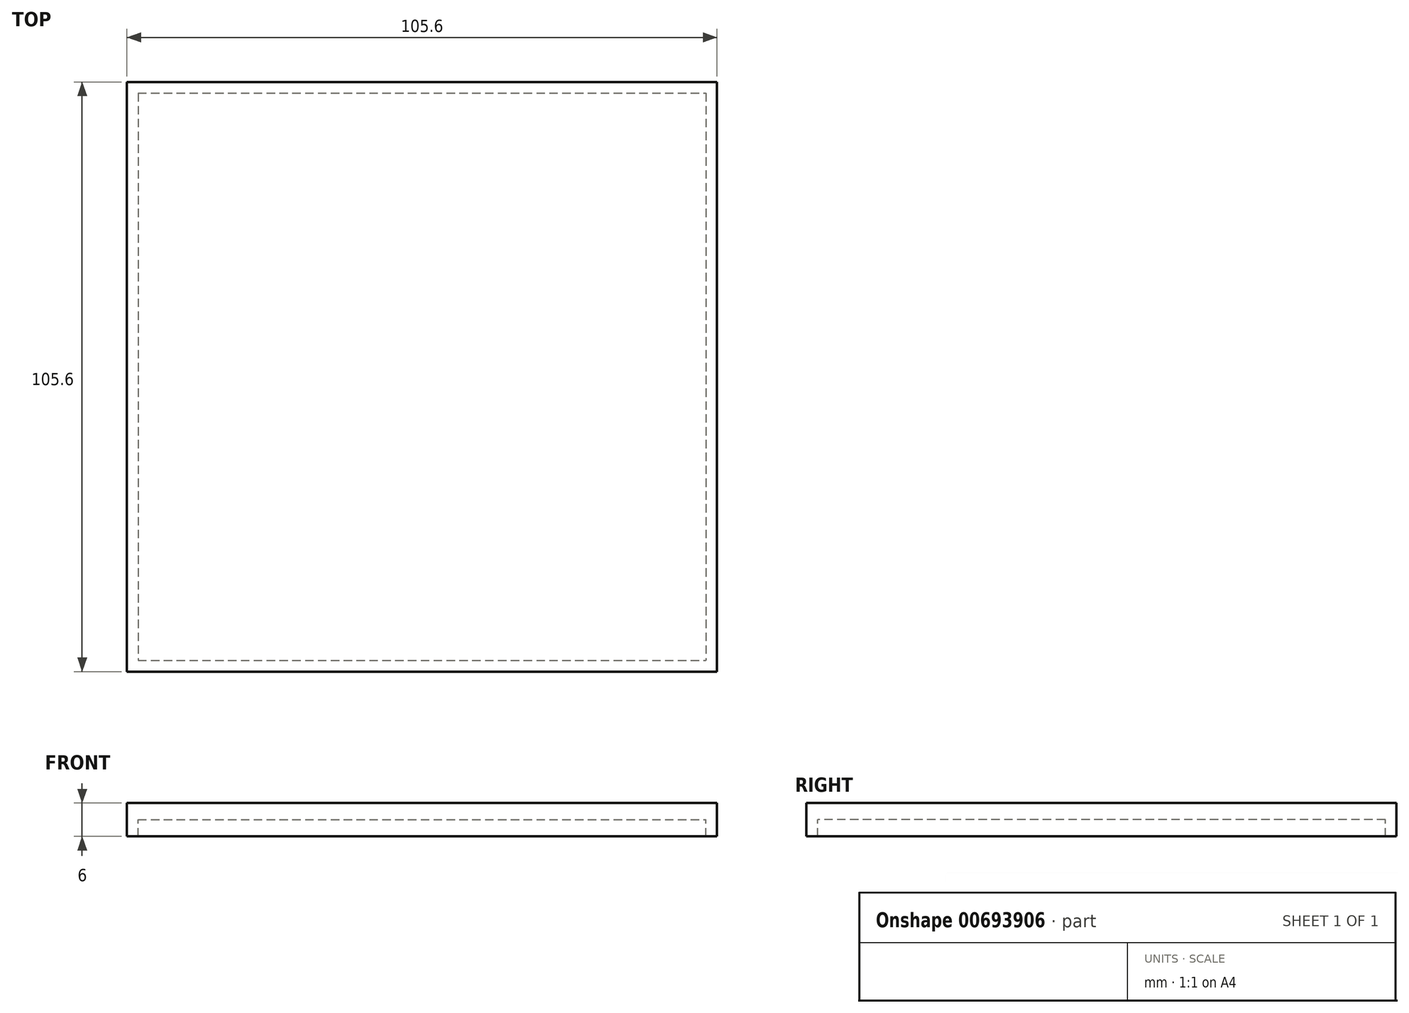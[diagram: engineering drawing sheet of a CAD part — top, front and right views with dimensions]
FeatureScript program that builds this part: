
annotation { "Feature Type Name" : "Feature", "Feature Type Description" : "" }
export const myFeature = defineFeature(function(context is Context, id is Id, definition is map)
    precondition{}
    {
        {
            var Q0;
            Q0=qCreatedBy(makeId("Top.planeOp"),FACE);
            var sketch = newSketch(context, id + "F0", { "sketchPlane" : qUnion([Q0])});
            skLineSegment(sketch, "E0.bottom", {"start": v(-50.8, 50.8) * mm, "end": v(50.8, 50.8) * mm});
            skLineSegment(sketch, "E0.top", {"start": v(-50.8, -50.8) * mm, "end": v(50.8, -50.8) * mm});
            skLineSegment(sketch, "E0.left", {"start": v(-50.8, 50.8) * mm, "end": v(-50.8, -50.8) * mm});
            skLineSegment(sketch, "E0.right", {"start": v(50.8, 50.8) * mm, "end": v(50.8, -50.8) * mm});
            skPoint(sketch, "E0.middle", {"position": v(0, 0) * mm});
            skLineSegment(sketch, "E1.0", {"start": v(-52.8, 52.8) * mm, "end": v(-52.8, -52.8) * mm});
            skLineSegment(sketch, "E1.1", {"start": v(-52.8, 52.8) * mm, "end": v(52.8, 52.8) * mm});
            skLineSegment(sketch, "E1.2", {"start": v(52.8, 52.8) * mm, "end": v(52.8, -52.8) * mm});
            skLineSegment(sketch, "E1.3", {"start": v(-52.8, -52.8) * mm, "end": v(52.8, -52.8) * mm});
            skSolve(sketch);
        }
        {
            var Q0;
            Q0=makeQuery(id+"F0.imprint","IMPRINT",FACE,{"disambiguationData":[TD([[makeQuery(id+"F0.imprint","IMPRINT",EDGE,{"derivedFrom":sQuery(id+"F0.wireOp",EDGE,"E0.bottom")}),1.0]])]});
            extrude(context, id + "F1", {"entities" : qUnion([Q0]), "oppositeDirection" : true, "depth" : 3 * mm, "offsetDistance" : 25.4 * mm});
        }
        {
            var Q0;
            Q0=qCreatedBy(makeId("Top.planeOp"),FACE);
            var sketch = newSketch(context, id + "F2", { "sketchPlane" : qUnion([Q0])});
            skLineSegment(sketch, "E2.bottom", {"start": v(-52.8, -52.8) * mm, "end": v(52.8, -52.8) * mm});
            skLineSegment(sketch, "E2.top", {"start": v(-52.8, 52.8) * mm, "end": v(52.8, 52.8) * mm});
            skLineSegment(sketch, "E2.left", {"start": v(-52.8, -52.8) * mm, "end": v(-52.8, 52.8) * mm});
            skLineSegment(sketch, "E2.right", {"start": v(52.8, -52.8) * mm, "end": v(52.8, 52.8) * mm});
            skSolve(sketch);
        }
        {
            var Q0;
            Q0 = qSketchRegion(id + "F2", true);
            extrude(context, id + "F3", {"entities" : qUnion([Q0]), "operationType" : NewBodyOperationType.ADD, "depth" : 3 * mm, "offsetDistance" : 25.4 * mm});
        }
    });
